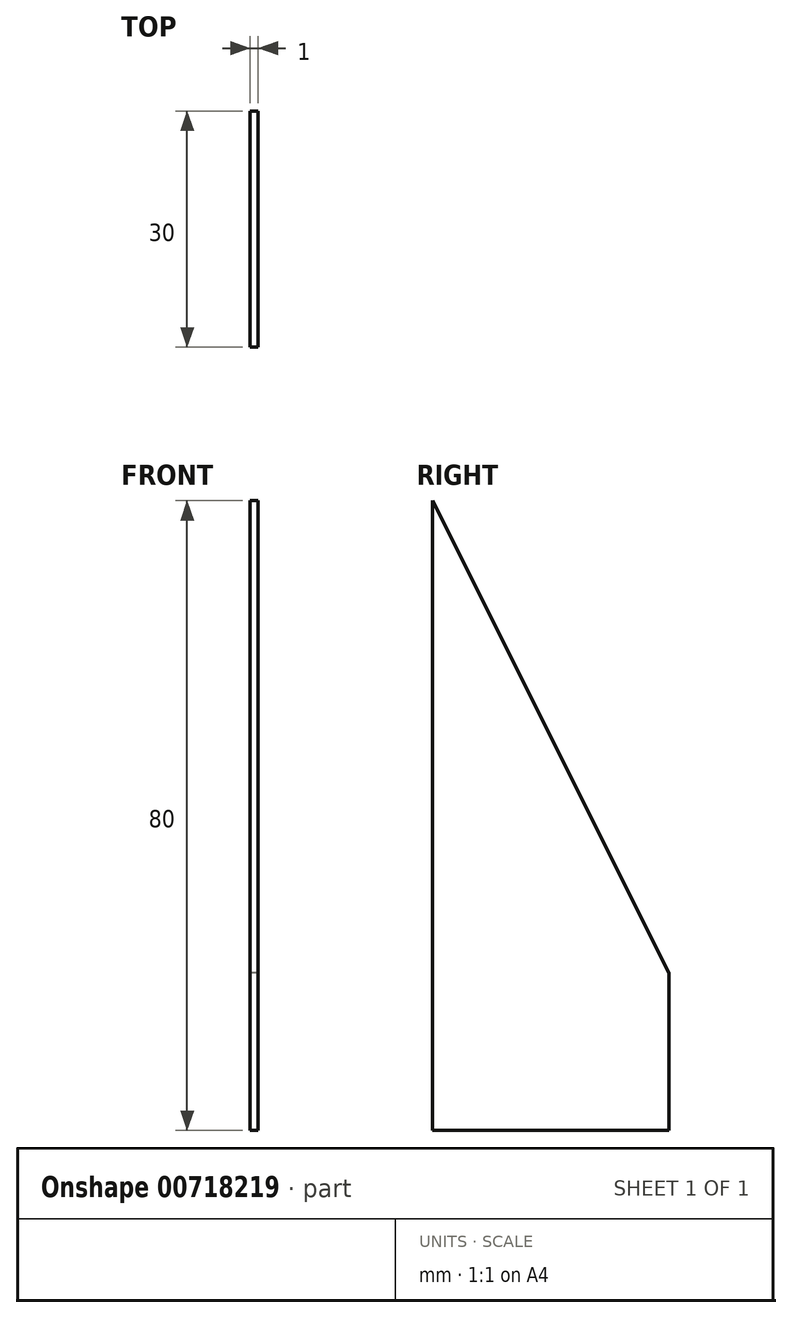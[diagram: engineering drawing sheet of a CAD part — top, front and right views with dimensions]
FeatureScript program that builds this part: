
annotation { "Feature Type Name" : "Feature", "Feature Type Description" : "" }
export const myFeature = defineFeature(function(context is Context, id is Id, definition is map)
    precondition{}
    {
        {
            var Q0;
            Q0=qCreatedBy(makeId("Right.planeOp"),FACE);
            var sketch = newSketch(context, id + "F0", { "sketchPlane" : qUnion([Q0])});
            skLineSegment(sketch, "E0.bottom", {"start": v(0, 80) * mm, "end": v(30, 80) * mm});
            skLineSegment(sketch, "E0.left", {"start": v(0, 80) * mm, "end": v(0, 160) * mm});
            skLineSegment(sketch, "E0.right", {"start": v(30, 80) * mm, "end": v(30, 100) * mm});
            skLineSegment(sketch, "E1", {"start": v(30, 100) * mm, "end": v(0, 100) * mm, "construction": true});
            skLineSegment(sketch, "E2", {"start": v(30, 100) * mm, "end": v(0, 160) * mm});
            skSolve(sketch);
        }
        {
            var Q0;
            Q0=makeQuery(id+"F0.imprint","IMPRINT",FACE,{"disambiguationData":[TD([[makeQuery(id+"F0.imprint","IMPRINT",EDGE,{"derivedFrom":sQuery(id+"F0.wireOp",EDGE,"E0.bottom")}),1.0]])]});
            extrude(context, id + "F1", {"entities" : qUnion([Q0]), "depth" : .5 * mm, "offsetDistance" : 25 * mm});
        }
        {
            var Q0;
            Q0=makeQuery(id+"F1.opExtrude","CAP_FACE",FACE,{"disambiguationData":[OSD([sQuery(id+"F0.wireOp",EDGE,"E0.bottom"),sQuery(id+"F0.wireOp",EDGE,"E0.left"),sQuery(id+"F0.wireOp",EDGE,"E0.right"),sQuery(id+"F0.wireOp",EDGE,"E2")])],"isStart":true});
            var Q1;
            Q1=makeQuery(id+"F1.opExtrude","CAP_FACE",FACE,{"disambiguationData":[OSD([sQuery(id+"F0.wireOp",EDGE,"E0.bottom"),sQuery(id+"F0.wireOp",EDGE,"E0.left"),sQuery(id+"F0.wireOp",EDGE,"E0.right"),sQuery(id+"F0.wireOp",EDGE,"E2"),sQuery(id+"F0.wireOp",EDGE,"sp9HEI1F-NEC0-a98b-AEu2-qCyFW6Tshl4p"),sQuery(id+"F0.wireOp",EDGE,"w7NNwwP4-B9RC-lpbD-7LMn-D5yA4eqohwqK"),sQuery(id+"F0.wireOp",EDGE,"6LwOThdF-OBeY-czWc-FXT9-IPJi8V7P1CQu"),sQuery(id+"F0.wireOp",EDGE,"abdaa649-2bb4-4492-8b38-bced2151a832.0.1.0"),sQuery(id+"F0.wireOp",EDGE,"abdaa649-2bb4-4492-8b38-bced2151a832.0.2.0"),sQuery(id+"F0.wireOp",EDGE,"abdaa649-2bb4-4492-8b38-bced2151a832.0.3.0"),sQuery(id+"F0.wireOp",EDGE,"abdaa649-2bb4-4492-8b38-bced2151a832.0.4.0")])],"isStart":false});
            extrude(context, id + "F2", {"entities" : qUnion([Q0, Q1]), "operationType" : NewBodyOperationType.ADD, "depth" : .5 * mm, "offsetDistance" : 25 * mm});
        }
    });
